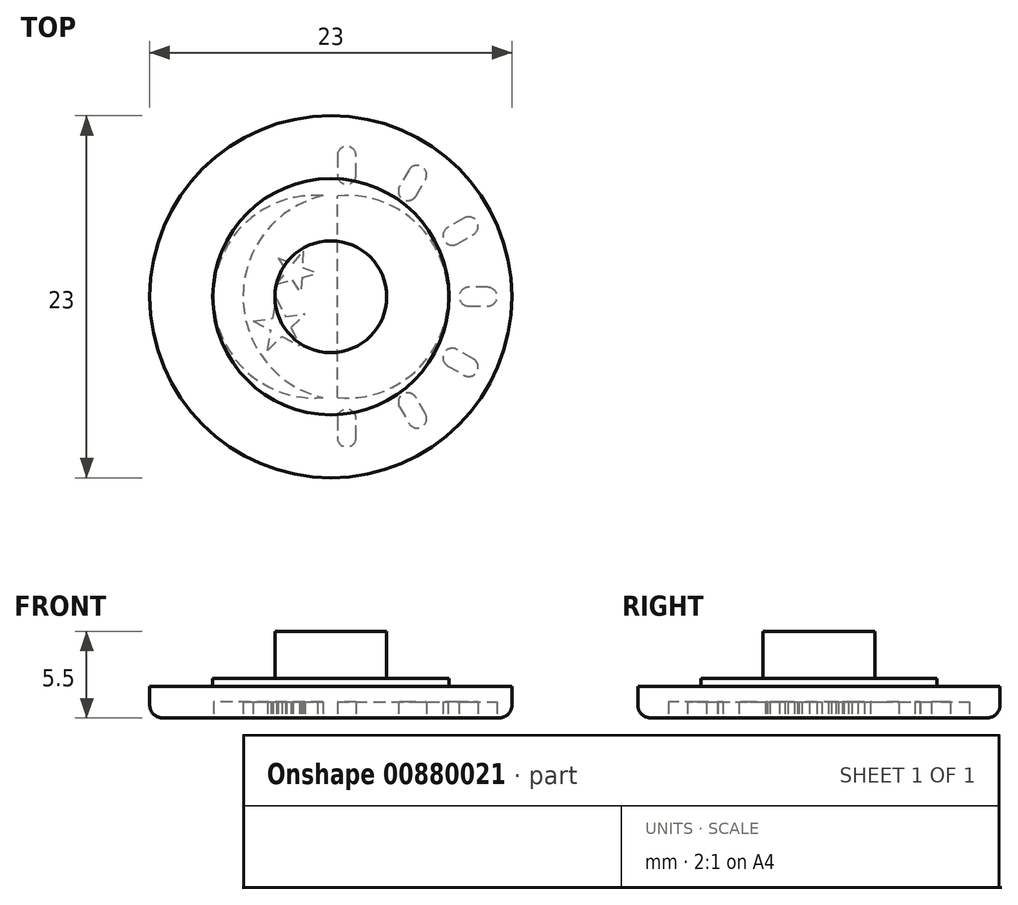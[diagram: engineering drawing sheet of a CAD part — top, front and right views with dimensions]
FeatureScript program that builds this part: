
annotation { "Feature Type Name" : "Feature", "Feature Type Description" : "" }
export const myFeature = defineFeature(function(context is Context, id is Id, definition is map)
    precondition{}
    {
        {
            var Q0;
            Q0=qCreatedBy(makeId("Top.planeOp"),FACE);
            var sketch = newSketch(context, id + "F0", { "sketchPlane" : qUnion([Q0])});
            skCircle(sketch, "E0", {"center": v(0, 0) * mm, "radius": 11.5 * mm});
            skSolve(sketch);
        }
        {
            var Q0;
            Q0=makeQuery(id+"F0.imprint","IMPRINT",FACE,{"disambiguationData":[TD([[makeQuery(id+"F0.imprint","IMPRINT",EDGE,{"derivedFrom":sQuery(id+"F0.wireOp",EDGE,"E0")}),1.0]])]});
            extrude(context, id + "F1", {"entities" : qUnion([Q0]), "depth" : 2 * mm, "offsetDistance" : 25 * mm});
        }
        {
            var Q0;
            Q0=makeQuery(id+"F1.opExtrude","CAP_FACE",FACE,{"disambiguationData":[OSD([sQuery(id+"F0.wireOp",EDGE,"E0")])],"isStart":false});
            var sketch = newSketch(context, id + "F2", { "sketchPlane" : qUnion([Q0])});
            skCircle(sketch, "E1", {"center": v(0, 0) * mm, "radius": 7.5 * mm});
            skSolve(sketch);
        }
        {
            var Q0;
            Q0=makeQuery(id+"F2.imprint","IMPRINT",FACE,{"disambiguationData":[TD([[makeQuery(id+"F2.imprint","IMPRINT",EDGE,{"derivedFrom":sQuery(id+"F2.wireOp",EDGE,"E1")}),1.0]])]});
            extrude(context, id + "F3", {"entities" : qUnion([Q0]), "operationType" : NewBodyOperationType.ADD, "depth" : .5 * mm, "offsetDistance" : 25 * mm});
        }
        {
            var Q0;
            Q0=makeQuery(id+"F3.opExtrude","CAP_FACE",FACE,{"disambiguationData":[OSD([sQuery(id+"F2.wireOp",EDGE,"E1")])],"isStart":false});
            var sketch = newSketch(context, id + "F4", { "sketchPlane" : qUnion([Q0])});
            skCircle(sketch, "E2", {"center": v(0, 0) * mm, "radius": 3.55 * mm});
            skSolve(sketch);
        }
        {
            var Q0;
            Q0=makeQuery(id+"F4.imprint","IMPRINT",FACE,{"disambiguationData":[TD([[makeQuery(id+"F4.imprint","IMPRINT",EDGE,{"derivedFrom":sQuery(id+"F4.wireOp",EDGE,"E2")}),1.0]])]});
            extrude(context, id + "F5", {"entities" : qUnion([Q0]), "operationType" : NewBodyOperationType.ADD, "depth" : 3 * mm, "offsetDistance" : 25 * mm});
        }
        {
            var Q0;
            Q0=makeQuery(id+"F1.opExtrude","CAP_FACE",FACE,{"disambiguationData":[OSD([sQuery(id+"F0.wireOp",EDGE,"E0")])],"isStart":true});
            var sketch = newSketch(context, id + "F6", { "sketchPlane" : qUnion([Q0])});
            skArc(sketch, "E3", {"start": v(-0.5, 6.42) * mm, "mid": v(-7.45, 0) * mm, "end": v(-0.5, -6.42) * mm});
            skArc(sketch, "E4", {"start": v(-0.5, 6.42) * mm, "mid": v(-5.58, 0) * mm, "end": v(-0.5, -6.42) * mm});
            skArc(sketch, "E5", {"start": v(1.01, -6.44) * mm, "mid": v(7.45, 0) * mm, "end": v(1.01, 6.44) * mm, "construction": true});
            skArc(sketch, "E6", {"start": v(1.61, 8.94) * mm, "mid": v(1.01, 9.54) * mm, "end": v(0.41, 8.94) * mm});
            skArc(sketch, "E7", {"start": v(0.41, 7.74) * mm, "mid": v(1.01, 7.14) * mm, "end": v(1.61, 7.74) * mm});
            skLineSegment(sketch, "E8", {"start": v(0.41, 7.74) * mm, "end": v(0.41, 8.94) * mm});
            skLineSegment(sketch, "E9", {"start": v(1.61, 8.94) * mm, "end": v(1.61, 7.74) * mm});
            skLineSegment(sketch, "E10", {"start": v(1.01, 0) * mm, "end": v(1.01, 13.63) * mm, "construction": true});
            skArc(sketch, "E11.1.0", {"start": v(4.36, 7) * mm, "mid": v(4.58, 6.19) * mm, "end": v(5.4, 6.4) * mm});
            skLineSegment(sketch, "E11.1.1", {"start": v(6, 7.44) * mm, "end": v(5.4, 6.4) * mm});
            skLineSegment(sketch, "E11.1.2", {"start": v(4.36, 7) * mm, "end": v(4.96, 8.04) * mm});
            skArc(sketch, "E11.1.3", {"start": v(6, 7.44) * mm, "mid": v(5.78, 8.26) * mm, "end": v(4.96, 8.04) * mm});
            skArc(sketch, "E11.2.0", {"start": v(7.42, 4.4) * mm, "mid": v(7.2, 3.57) * mm, "end": v(8.02, 3.35) * mm});
            skLineSegment(sketch, "E11.2.1", {"start": v(9.06, 3.95) * mm, "end": v(8.02, 3.35) * mm});
            skLineSegment(sketch, "E11.2.2", {"start": v(7.42, 4.4) * mm, "end": v(8.46, 5) * mm});
            skArc(sketch, "E11.2.3", {"start": v(9.06, 3.95) * mm, "mid": v(9.28, 4.77) * mm, "end": v(8.46, 5) * mm});
            skArc(sketch, "E11.3.0", {"start": v(8.75, 0.6) * mm, "mid": v(8.15, 0) * mm, "end": v(8.75, -0.6) * mm});
            skLineSegment(sketch, "E11.3.1", {"start": v(9.95, -0.6) * mm, "end": v(8.75, -0.6) * mm});
            skLineSegment(sketch, "E11.3.2", {"start": v(8.75, 0.6) * mm, "end": v(9.95, 0.6) * mm});
            skArc(sketch, "E11.3.3", {"start": v(9.95, -0.6) * mm, "mid": v(10.55, 0) * mm, "end": v(9.95, 0.6) * mm});
            skArc(sketch, "E11.4.0", {"start": v(8.02, -3.35) * mm, "mid": v(7.2, -3.57) * mm, "end": v(7.42, -4.4) * mm});
            skLineSegment(sketch, "E11.4.1", {"start": v(8.46, -5) * mm, "end": v(7.42, -4.4) * mm});
            skLineSegment(sketch, "E11.4.2", {"start": v(8.02, -3.35) * mm, "end": v(9.06, -3.95) * mm});
            skArc(sketch, "E11.4.3", {"start": v(8.46, -5) * mm, "mid": v(9.28, -4.77) * mm, "end": v(9.06, -3.95) * mm});
            skArc(sketch, "E11.5.0", {"start": v(5.4, -6.4) * mm, "mid": v(4.58, -6.19) * mm, "end": v(4.36, -7) * mm});
            skLineSegment(sketch, "E11.5.1", {"start": v(4.96, -8.04) * mm, "end": v(4.36, -7) * mm});
            skLineSegment(sketch, "E11.5.2", {"start": v(5.4, -6.4) * mm, "end": v(6, -7.44) * mm});
            skArc(sketch, "E11.5.3", {"start": v(4.96, -8.04) * mm, "mid": v(5.78, -8.26) * mm, "end": v(6, -7.44) * mm});
            skArc(sketch, "E11.6.0", {"start": v(1.61, -7.74) * mm, "mid": v(1.01, -7.14) * mm, "end": v(0.41, -7.74) * mm});
            skLineSegment(sketch, "E11.6.1", {"start": v(0.41, -8.94) * mm, "end": v(0.41, -7.74) * mm});
            skLineSegment(sketch, "E11.6.2", {"start": v(1.61, -7.74) * mm, "end": v(1.61, -8.94) * mm});
            skArc(sketch, "E11.6.3", {"start": v(0.41, -8.94) * mm, "mid": v(1.01, -9.54) * mm, "end": v(1.61, -8.94) * mm});
            skLineSegment(sketch, "E11.anchor1", {"start": v(1.01, 0) * mm, "end": v(0.41, 7.74) * mm, "construction": true});
            skLineSegment(sketch, "E11.anchor2", {"start": v(1.01, 0) * mm, "end": v(1.61, -7.74) * mm, "construction": true});
            skLineSegment(sketch, "E12", {"start": v(1.01, 6.44) * mm, "end": v(1.01, -6.44) * mm});
            skLineSegment(sketch, "E13", {"start": v(0.41, 8.94) * mm, "end": v(0.41, -7.74) * mm});
            skArc(sketch, "E14", {"start": v(0.41, -6.4) * mm, "mid": v(7.45, 0) * mm, "end": v(0.41, 6.4) * mm});
            skCircle(sketch, "E15.cCircle", {"center": v(-3.2, 1.85) * mm, "radius": 1.42 * mm, "construction": true});
            skLineSegment(sketch, "E15.0", {"start": v(-1.62, 1.08) * mm, "end": v(-3.45, 0.11) * mm, "construction": true});
            skLineSegment(sketch, "E15.1", {"start": v(-3.45, 0.11) * mm, "end": v(-4.93, 1.55) * mm, "construction": true});
            skLineSegment(sketch, "E15.2", {"start": v(-4.93, 1.55) * mm, "end": v(-4.02, 3.4) * mm, "construction": true});
            skLineSegment(sketch, "E15.3", {"start": v(-4.02, 3.4) * mm, "end": v(-1.98, 3.11) * mm, "construction": true});
            skLineSegment(sketch, "E15.4", {"start": v(-1.98, 3.11) * mm, "end": v(-1.62, 1.08) * mm, "construction": true});
            skPoint(sketch, "E15.0.midPoint", {"position": v(-2.54, 0.6) * mm});
            skLineSegment(sketch, "E16", {"start": v(-4.93, 1.55) * mm, "end": v(-1.98, 3.11) * mm});
            skLineSegment(sketch, "E17", {"start": v(-3.45, 0.11) * mm, "end": v(-1.98, 3.11) * mm});
            skLineSegment(sketch, "E18", {"start": v(-4.02, 3.4) * mm, "end": v(-3.45, 0.11) * mm});
            skLineSegment(sketch, "E19", {"start": v(-4.02, 3.4) * mm, "end": v(-1.62, 1.08) * mm});
            skLineSegment(sketch, "E20", {"start": v(-4.93, 1.55) * mm, "end": v(-1.62, 1.08) * mm});
            skCircle(sketch, "E21.cCircle", {"center": v(-2.26, -1.57) * mm, "radius": 1.15 * mm, "construction": true});
            skLineSegment(sketch, "E21.0", {"start": v(-0.85, -1.5) * mm, "end": v(-1.75, -2.9) * mm, "construction": true});
            skLineSegment(sketch, "E21.1", {"start": v(-1.75, -2.9) * mm, "end": v(-3.36, -2.46) * mm, "construction": true});
            skLineSegment(sketch, "E21.2", {"start": v(-3.36, -2.46) * mm, "end": v(-3.45, -0.8) * mm, "construction": true});
            skLineSegment(sketch, "E21.3", {"start": v(-3.45, -0.8) * mm, "end": v(-1.9, -0.2) * mm, "construction": true});
            skLineSegment(sketch, "E21.4", {"start": v(-1.9, -0.2) * mm, "end": v(-0.85, -1.5) * mm, "construction": true});
            skLineSegment(sketch, "E22", {"start": v(-3.36, -2.46) * mm, "end": v(-1.9, -0.2) * mm});
            skLineSegment(sketch, "E23", {"start": v(-1.75, -2.9) * mm, "end": v(-1.9, -0.2) * mm});
            skLineSegment(sketch, "E24", {"start": v(-3.45, -0.8) * mm, "end": v(-1.75, -2.9) * mm});
            skLineSegment(sketch, "E25", {"start": v(-3.45, -0.8) * mm, "end": v(-0.85, -1.5) * mm});
            skLineSegment(sketch, "E26", {"start": v(-3.36, -2.46) * mm, "end": v(-0.85, -1.5) * mm});
            skSolve(sketch);
        }
        {
            var Q0;
            Q0=qSketchRegion(id+"F6",true);
            extrude(context, id + "F7", {"entities" : qUnion([Q0]), "operationType" : NewBodyOperationType.REMOVE, "depth" : -1 * mm, "offsetDistance" : 25 * mm});
        }
        {
            var Q0;
            Q0=makeQuery(id+"F1.opExtrude","CAP_EDGE",EDGE,{"disambiguationData":[OSD([sQuery(id+"F0.wireOp",EDGE,"E0")])],"isStart":true});
            fillet(context, id + "F8", {"entities" : qUnion([Q0]), "radius" : .8 * mm, "tangentPropagation" : true, "allowEdgeOverflow" : false});
        }
    });
